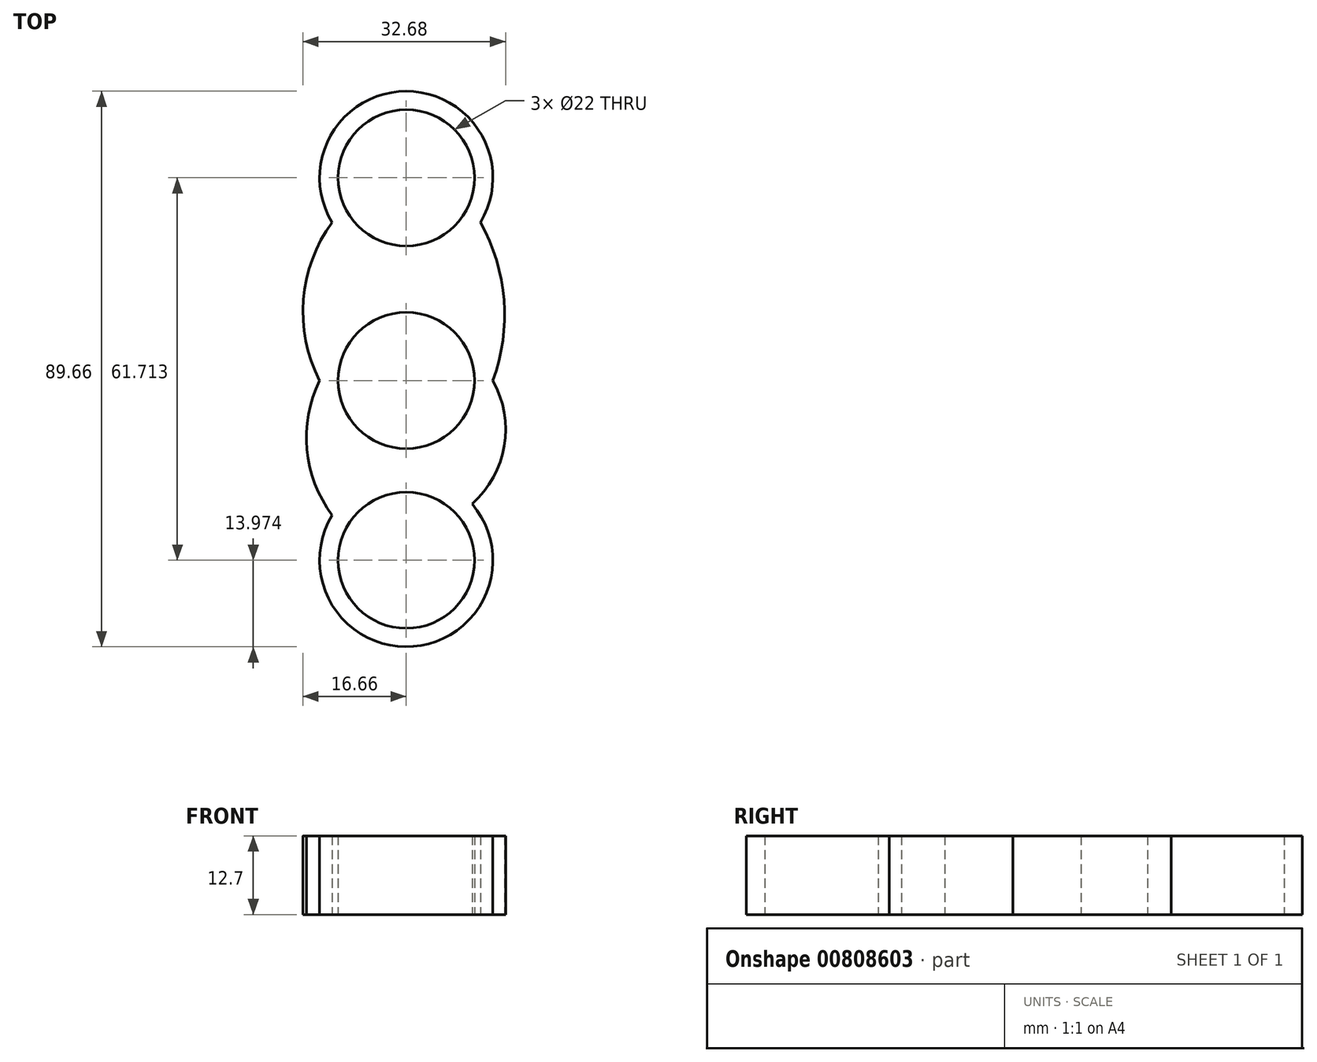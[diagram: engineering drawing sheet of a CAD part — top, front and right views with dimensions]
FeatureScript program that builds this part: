
annotation { "Feature Type Name" : "Feature", "Feature Type Description" : "" }
export const myFeature = defineFeature(function(context is Context, id is Id, definition is map)
    precondition{}
    {
        {
            var Q0;
            Q0=qCreatedBy(makeId("Top.planeOp"),FACE);
            var sketch = newSketch(context, id + "F0", { "sketchPlane" : qUnion([Q0])});
            skCircle(sketch, "E0", {"center": v(0, 0) * mm, "radius": 44.45 * mm});
            skCircle(sketch, "E1", {"center": v(0, 0) * mm, "radius": 11 * mm});
            skCircle(sketch, "E2", {"center": v(0, 32.72) * mm, "radius": 11 * mm});
            skCircle(sketch, "E3", {"center": v(0, -29) * mm, "radius": 11 * mm});
            skCircle(sketch, "E4", {"center": v(0, 32.72) * mm, "radius": 13.97 * mm});
            skCircle(sketch, "E5", {"center": v(0, -29) * mm, "radius": 13.97 * mm});
            skCircle(sketch, "E6", {"center": v(0, 0) * mm, "radius": 13.97 * mm});
            skArc(sketch, "E7", {"start": v(-11.97, 25.5) * mm, "mid": v(-16.58, 13.04) * mm, "end": v(-13.97, 0) * mm});
            skArc(sketch, "E8", {"start": v(-13.97, 0) * mm, "mid": v(-16.02, -11.15) * mm, "end": v(-11.93, -21.73) * mm});
            skArc(sketch, "E9", {"start": v(13.97, 0) * mm, "mid": v(15.76, 12.97) * mm, "end": v(11.97, 25.5) * mm});
            skArc(sketch, "E10", {"start": v(10.62, -19.92) * mm, "mid": v(15.8, -10.55) * mm, "end": v(13.97, 0) * mm});
            skSolve(sketch);
        }
        {
            var Q0;
            Q0=makeQuery(id+"F0.imprint","IMPRINT",FACE,{"disambiguationData":[TD([[makeQuery(id+"F0.imprint","IMPRINT",EDGE,{"derivedFrom":sQuery(id+"F0.wireOp",EDGE,"E2")}),-1.0]])]});
            var Q1;
            {var subQ0=sQuery(id+"F0.wireOp",EDGE,"E4");var subQ1=sQuery(id+"F0.wireOp",EDGE,"E0");var subQ2=makeQuery(id+"F0.imprint","INTERSECT",VERTEX,{"disambiguationData":[OD(0.0)],"derivedFrom":[subQ1,subQ0]});Q1=makeQuery(id+"F0.imprint","IMPRINT",FACE,{"disambiguationData":[TD([[makeQuery(id+"F0.imprint","IMPRINT",EDGE,{"disambiguationData":[TD([[subQ2,1.0]])],"derivedFrom":subQ1}),-1.0]])]});}
            var Q2;
            Q2=makeQuery(id+"F0.imprint","IMPRINT",FACE,{"disambiguationData":[TD([[makeQuery(id+"F0.imprint","IMPRINT",EDGE,{"derivedFrom":sQuery(id+"F0.wireOp",EDGE,"E1")}),-1.0]])]});
            var Q3;
            Q3=makeQuery(id+"F0.imprint","IMPRINT",FACE,{"disambiguationData":[TD([[makeQuery(id+"F0.imprint","IMPRINT",EDGE,{"derivedFrom":sQuery(id+"F0.wireOp",EDGE,"E3")}),-1.0]])]});
            var Q4;
            {var subQ0=sQuery(id+"F0.wireOp",EDGE,"E8");Q4=makeQuery(id+"F0.imprint","IMPRINT",FACE,{"disambiguationData":[TD([[makeQuery(id+"F0.imprint","IMPRINT",EDGE,{"derivedFrom":subQ0}),1.0]])]});}
            var Q5;
            {var subQ0=sQuery(id+"F0.wireOp",EDGE,"E7");Q5=makeQuery(id+"F0.imprint","IMPRINT",FACE,{"disambiguationData":[TD([[makeQuery(id+"F0.imprint","IMPRINT",EDGE,{"derivedFrom":subQ0}),1.0]])]});}
            extrude(context, id + "F1", {"entities" : qUnion([Q0, Q1, Q2, Q3, Q4, Q5]), "depth" : 12.7 * mm, "offsetDistance" : 25.4 * mm});
        }
    });
